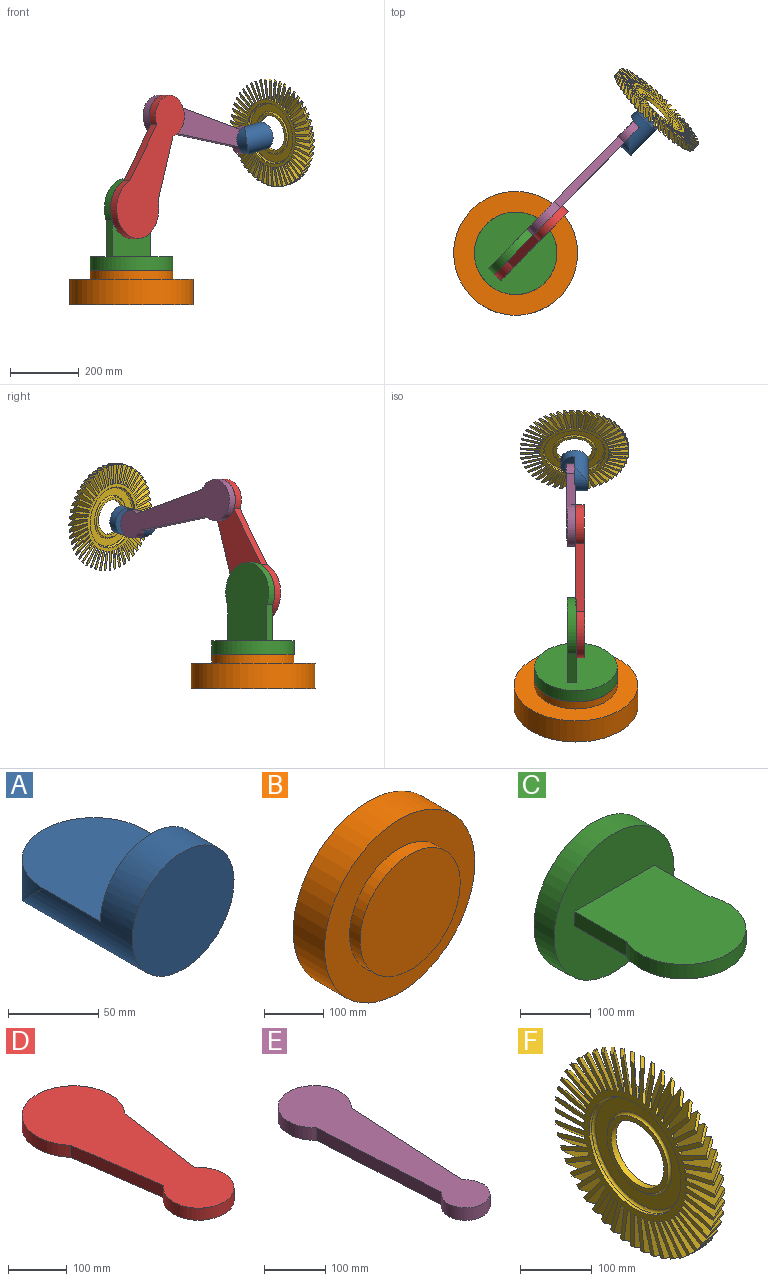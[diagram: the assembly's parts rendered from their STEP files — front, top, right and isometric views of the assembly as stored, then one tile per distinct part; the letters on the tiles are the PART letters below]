
ASSEMBLY  parts=6 mates=5
PART A: 5 faces, bbox 80x110x80 mm
  f0: plane 80x40mm, normal (0,1,0), area 2513.3mm2, adj f1,f3
  f1: cylinder r=40mm len=110mm, axis (0,-1,0), area 15138.1mm2, adj f0,f2,f3,f4
  f2: plane 80x80mm, normal (0,-1,0), area 5026.5mm2, adj f1
  f3: plane 85x80mm, normal (0,0,1), area 6113.3mm2, adj f0,f1,f4
  f4: cylinder r=40mm len=80mm, axis (0,0,1), area 3200mm2, adj f1,f3
PART B: 5 faces, bbox 360x100x360 mm
  f0: plane 240x240mm, normal (0,-1,0), area 45238.9mm2, adj f1
  f1: cylinder r=120mm len=240mm, axis (0,1,0), area 18849.6mm2, adj f0,f2
  f2: plane 360x360mm, normal (0,-1,0), area 56548.7mm2, adj f1,f3
  f3: cylinder r=180mm len=360mm, axis (0,1,0), area 84823mm2, adj f2,f4
  f4: plane 360x360mm, normal (0,1,0), area 101787.6mm2, adj f3
PART C: 8 faces, bbox 240x267.5x240 mm
  f0: plane 104.56x25mm, normal (-1,0,0), area 2613.9mm2, adj f1,f3,f4,f7
  f1: cylinder r=87.5mm len=175mm, axis (0,0,-1), area 8696.9mm2, adj f0,f2,f3,f4
  f2: plane 104.56x25mm, normal (1,0,0), area 2613.9mm2, adj f1,f3,f4,f7
  f3: plane 227.5x175mm, normal (0,0,1), area 34784mm2, adj f0,f1,f2,f7
  f4: plane 227.5x175mm, normal (0,0,-1), area 34784mm2, adj f0,f1,f2,f7
  f5: cylinder r=120mm len=240mm, axis (0,-1,0), area 30159.3mm2, adj f6,f7
  f6: plane 240x240mm, normal (0,1,0), area 45238.9mm2, adj f5
  f7: plane 240x240mm, normal (0,-1,0), area 41238.9mm2, adj f0,f2,f3,f4,f5
PART D: 6 faces, bbox 175x447.5x25 mm
  f0: cylinder r=87.5mm len=175mm, axis (0,0,1), area 10081.2mm2, adj f1,f3,f4,f5
  f1: plane 194.59x27.5mm, normal (-0.99,-0.14,0), area 4913mm2, adj f0,f2,f4,f5
  f2: cylinder r=60mm len=120mm, axis (0,0,1), area 7399.4mm2, adj f1,f3,f4,f5
  f3: plane 194.59x27.5mm, normal (0.99,-0.14,0), area 4913mm2, adj f0,f2,f4,f5
  f4: plane 447.5x175mm, normal (0,0,-1), area 52030.2mm2, adj f0,f1,f2,f3
  f5: plane 447.5x175mm, normal (0,0,1), area 52030.2mm2, adj f0,f1,f2,f3
PART E: 6 faces, bbox 120x450x25 mm
  f0: cylinder r=60mm len=120mm, axis (0,0,-1), area 7235.6mm2, adj f1,f3,f4,f5
  f1: plane 274.05x25mm, normal (-1,-0.05,0), area 6861.6mm2, adj f0,f2,f4,f5
  f2: cylinder r=40mm len=80mm, axis (0,0,-1), area 4932.9mm2, adj f1,f3,f4,f5
  f3: plane 274.05x25mm, normal (1,-0.05,0), area 6861.6mm2, adj f0,f2,f4,f5
  f4: plane 450x120mm, normal (0,0,1), area 33012mm2, adj f0,f1,f2,f3
  f5: plane 450x120mm, normal (0,0,-1), area 33012mm2, adj f0,f1,f2,f3
PART F: 209 faces, bbox 20.3x315.4x315.3 mm
  f0: torus R=86.5mm, axis (-1,0,0), area 3515.4mm2, adj f7,f203
  f1: torus R=64mm, axis (-1,0,0), area 2426.1mm2, adj f207,f208
  f2: torus R=64mm, axis (-1,0,0), area 2426.1mm2, adj f9,f203
  f3: cylinder r=157.5mm len=21.71mm, axis (1,0,0), area 130.3mm2, adj f6,f176,f177,f204
  f4: plane 22.36x20mm, normal (0,0.49,0.87), area 113.1mm2, adj f6,f12,f176,f204
  f5: cylinder r=157.5mm len=25.8mm, axis (1,0,0), area 130.3mm2, adj f6,f180,f204,f206
  f6: plane 314.98x314.86mm, normal (1,0,0), area 25655mm2, adj f3,f4,f5,f7,f12,f13,f14,f15
  f7: cylinder r=90.5mm len=181mm, axis (1,0,0), area 2843.1mm2, adj f0,f6
  f8: cylinder r=90.5mm len=181mm, axis (1,0,0), area 2843.1mm2, adj f11,f204
  f9: plane 120x120mm, normal (1,0,0), area 2814.9mm2, adj f2,f10
  f10: cylinder r=52mm len=104mm, axis (1,0,0), area 3267.3mm2, adj f9,f207
  f11: torus R=86.5mm, axis (-1,0,0), area 3515.5mm2, adj f8,f208
  f12: plane 61.08x41.82mm, normal (-0.71,0.64,-0.3), area 1610.9mm2, adj f4,f6,f19,f204
  f13: plane 24.82x20mm, normal (0,0.25,0.97), area 113.1mm2, adj f6,f14,f204,f206
  f14: plane 59.47x37.51mm, normal (0.71,-0.67,0.23), area 1598.6mm2, adj f6,f13,f15,f204
  f15: cylinder r=157.5mm len=24.84mm, axis (1,0,0), area 130.3mm2, adj f6,f14,f16,f204
  f16: plane 61.46x36.15mm, normal (-0.71,0.67,-0.22), area 1610.9mm2, adj f6,f15,f17,f204
  f17: plane 23.78x20mm, normal (0,0.38,0.93), area 113.1mm2, adj f6,f16,f18,f204
  f18: plane 59.11x43.29mm, normal (0.71,-0.64,0.31), area 1598.6mm2, adj f6,f17,f19,f204
  f19: cylinder r=157.5mm len=23.47mm, axis (1,0,0), area 130.3mm2, adj f6,f12,f18,f204
  f20: cylinder r=157.5mm len=26.34mm, axis (1,0,0), area 130.3mm2, adj f6,f21,f22,f204
  f21: plane 59.19x23.14mm, normal (-0.71,0.71,-0.04), area 1610.9mm2, adj f6,f20,f204,f205
  f22: plane 57.28x24.22mm, normal (0.71,-0.71,0.05), area 1598.6mm2, adj f6,f20,f181,f204
  f23: cylinder r=157.5mm len=26.45mm, axis (1,0,0), area 130.2mm2, adj f6,f24,f25,f204
  f24: plane 57.01x24.01mm, normal (-0.71,0.71,0.05), area 1610.9mm2, adj f6,f23,f181,f204
  f25: plane 58.43x23.45mm, normal (0.71,-0.71,-0.04), area 1598.6mm2, adj f6,f23,f202,f204
  f26: cylinder r=157.5mm len=26.13mm, axis (1,0,0), area 130.3mm2, adj f6,f27,f28,f204
  f27: plane 58.39x31.06mm, normal (-0.71,0.69,0.14), area 1610.9mm2, adj f6,f26,f202,f204
  f28: plane 60.04x30.2mm, normal (0.71,-0.7,-0.13), area 1598.6mm2, adj f6,f26,f155,f204
  f29: cylinder r=157.5mm len=25.37mm, axis (1,0,0), area 130.3mm2, adj f6,f30,f31,f204
  f30: plane 59.01x37.59mm, normal (-0.71,0.67,0.23), area 1610.9mm2, adj f6,f29,f155,f204
  f31: plane 60.71x36.48mm, normal (0.71,-0.67,-0.22), area 1598.6mm2, adj f6,f29,f201,f204
  f32: cylinder r=157.5mm len=24.2mm, axis (1,0,0), area 130.3mm2, adj f6,f33,f34,f204
  f33: plane 58.66x43.5mm, normal (-0.71,0.64,0.31), area 1610.9mm2, adj f6,f32,f201,f204
  f34: plane 60.38x42.17mm, normal (0.71,-0.64,-0.3), area 1598.6mm2, adj f6,f32,f156,f204
  f35: cylinder r=157.5mm len=22.63mm, axis (1,0,0), area 130.3mm2, adj f6,f36,f37,f204
  f36: plane 57.35x48.69mm, normal (-0.71,0.59,0.39), area 1610.9mm2, adj f6,f35,f156,f204
  f37: plane 59.07x47.18mm, normal (0.71,-0.6,-0.38), area 1598.6mm2, adj f6,f35,f200,f204
  f38: cylinder r=157.5mm len=20.69mm, axis (1,0,0), area 130.3mm2, adj f6,f39,f40,f204
  f39: plane 55.1x53.09mm, normal (-0.71,0.54,0.46), area 1610.9mm2, adj f6,f38,f200,f204
  f40: plane 56.8x51.41mm, normal (0.71,-0.54,-0.46), area 1598.6mm2, adj f6,f38,f157,f204
  f41: cylinder r=157.5mm len=20mm, axis (1,0,0), area 130.3mm2, adj f6,f42,f43,f204
  f42: plane 56.61x51.94mm, normal (-0.71,0.47,0.53), area 1610.9mm2, adj f6,f41,f157,f204
  f43: plane 54.81x53.59mm, normal (0.71,-0.48,-0.52), area 1601.4mm2, adj f6,f41,f199,f204
  f44: cylinder r=157.5mm len=21.21mm, axis (1,0,0), area 130.3mm2, adj f6,f45,f46,f204
  f45: plane 59.21x47.93mm, normal (-0.71,0.4,0.58), area 1610.9mm2, adj f6,f44,f199,f204
  f46: plane 57.3x49.52mm, normal (0.71,-0.41,-0.58), area 1601.4mm2, adj f6,f44,f158,f204
  f47: cylinder r=157.5mm len=23.06mm, axis (1,0,0), area 130.3mm2, adj f6,f48,f49,f204
  f48: plane 60.83x43.14mm, normal (-0.71,0.32,0.63), area 1610.9mm2, adj f6,f47,f158,f204
  f49: plane 58.87x44.63mm, normal (0.71,-0.33,-0.63), area 1601.4mm2, adj f6,f47,f198,f204
  f50: cylinder r=157.5mm len=24.53mm, axis (1,0,0), area 130.3mm2, adj f6,f51,f52,f204
  f51: plane 61.46x37.63mm, normal (-0.71,0.24,0.67), area 1610.9mm2, adj f6,f50,f198,f204
  f52: plane 59.47x39.02mm, normal (0.71,-0.25,-0.66), area 1601.4mm2, adj f6,f50,f159,f204
  f53: cylinder r=157.5mm len=25.6mm, axis (1,0,0), area 130.3mm2, adj f6,f54,f55,f204
  f54: plane 61.07x31.51mm, normal (-0.71,0.15,0.69), area 1610.9mm2, adj f6,f53,f159,f204
  f55: plane 59.1x32.77mm, normal (0.71,-0.16,-0.69), area 1601.4mm2, adj f6,f53,f197,f204
  f56: cylinder r=157.5mm len=26.25mm, axis (1,0,0), area 130.3mm2, adj f6,f57,f58,f204
  f57: plane 59.69x24.87mm, normal (-0.71,0.06,0.71), area 1610.9mm2, adj f6,f56,f197,f204
  f58: plane 57.76x25.98mm, normal (0.71,-0.07,-0.7), area 1601.4mm2, adj f6,f56,f160,f204
  f59: cylinder r=157.5mm len=26.47mm, axis (1,0,0), area 130.3mm2, adj f6,f60,f61,f204
  f60: plane 57.49x22.2mm, normal (-0.71,-0.03,0.71), area 1610.9mm2, adj f6,f59,f160,f204
  f61: plane 57.98x21.66mm, normal (0.71,0.02,-0.71), area 1601.4mm2, adj f6,f59,f196,f204
  f62: cylinder r=157.5mm len=26.25mm, axis (1,0,0), area 130.3mm2, adj f6,f63,f64,f204
  f63: plane 58.09x29.35mm, normal (-0.71,-0.12,0.7), area 1610.9mm2, adj f6,f62,f196,f204
  f64: plane 59.72x28.54mm, normal (0.71,0.11,-0.7), area 1601.4mm2, adj f6,f62,f161,f204
  f65: cylinder r=157.5mm len=25.6mm, axis (1,0,0), area 130.3mm2, adj f6,f66,f67,f204
  f66: plane 58.95x36.01mm, normal (-0.71,-0.21,0.68), area 1610.9mm2, adj f6,f65,f161,f204
  f67: plane 60.63x34.96mm, normal (0.71,0.2,-0.68), area 1601.4mm2, adj f6,f65,f195,f204
  f68: cylinder r=157.5mm len=24.53mm, axis (1,0,0), area 130.3mm2, adj f6,f69,f70,f204
  f69: plane 58.84x42.08mm, normal (-0.71,-0.29,0.65), area 1610.9mm2, adj f6,f68,f195,f204
  f70: plane 60.56x40.81mm, normal (0.71,0.28,-0.65), area 1601.4mm2, adj f6,f68,f162,f204
  f71: cylinder r=157.5mm len=23.06mm, axis (1,0,0), area 130.3mm2, adj f6,f72,f73,f204
  f72: plane 57.77x47.46mm, normal (-0.71,-0.37,0.6), area 1610.9mm2, adj f6,f71,f162,f204
  f73: plane 59.49x45.99mm, normal (0.71,0.36,-0.61), area 1601.4mm2, adj f6,f71,f194,f204
  f74: cylinder r=157.5mm len=21.21mm, axis (1,0,0), area 130.3mm2, adj f6,f75,f76,f204
  f75: plane 55.75x52.07mm, normal (-0.71,-0.45,0.55), area 1610.9mm2, adj f6,f74,f194,f204
  f76: plane 57.45x50.43mm, normal (0.71,0.44,-0.56), area 1601.4mm2, adj f6,f74,f163,f204
  f77: cylinder r=157.5mm len=20mm, axis (1,0,0), area 130.3mm2, adj f6,f78,f79,f204
  f78: plane 55.82x52.81mm, normal (-0.71,-0.51,0.49), area 1610.9mm2, adj f6,f77,f163,f204
  f79: plane 54.48x54.04mm, normal (0.71,0.51,-0.5), area 1601.4mm2, adj f6,f77,f193,f204
  f80: cylinder r=157.5mm len=20.7mm, axis (1,0,0), area 130.3mm2, adj f6,f81,f82,f204
  f81: plane 58.65x49.01mm, normal (-0.71,-0.57,0.42), area 1610.9mm2, adj f6,f80,f193,f204
  f82: plane 56.77x50.61mm, normal (0.71,0.56,-0.43), area 1601.4mm2, adj f6,f80,f164,f204
  f83: cylinder r=157.5mm len=22.64mm, axis (1,0,0), area 130.3mm2, adj f6,f84,f85,f204
  f84: plane 60.52x44.4mm, normal (-0.71,-0.62,0.34), area 1610.9mm2, adj f6,f83,f164,f204
  f85: plane 58.57x45.92mm, normal (0.71,0.61,-0.35), area 1601.4mm2, adj f6,f83,f192,f204
  f86: cylinder r=157.5mm len=24.2mm, axis (1,0,0), area 130.3mm2, adj f6,f87,f88,f204
  f87: plane 61.39x39.07mm, normal (-0.71,-0.66,0.26), area 1610.9mm2, adj f6,f86,f192,f204
  f88: plane 59.41x40.48mm, normal (0.71,0.65,-0.27), area 1601.4mm2, adj f6,f86,f165,f204
  f89: cylinder r=157.5mm len=25.37mm, axis (1,0,0), area 130.3mm2, adj f6,f90,f91,f204
  f90: plane 61.26x33.09mm, normal (-0.71,-0.69,0.18), area 1610.9mm2, adj f6,f89,f165,f204
  f91: plane 59.28x34.38mm, normal (0.71,0.68,-0.18), area 1601.4mm2, adj f6,f89,f191,f204
  f92: cylinder r=157.5mm len=26.13mm, axis (1,0,0), area 130.3mm2, adj f6,f93,f94,f204
  f93: plane 60.13x26.57mm, normal (-0.71,-0.7,0.09), area 1610.9mm2, adj f6,f92,f191,f204
  f94: plane 58.19x27.72mm, normal (0.71,0.7,-0.1), area 1601.4mm2, adj f6,f92,f166,f204
  f95: cylinder r=157.5mm len=26.45mm, axis (1,0,0), area 130.3mm2, adj f6,f96,f97,f204
  f96: plane 58.03x20.35mm, normal (-0.71,-0.71,0), area 1610.9mm2, adj f6,f95,f166,f204
  f97: plane 57.66x20.61mm, normal (0.71,0.71,0), area 1601.4mm2, adj f6,f95,f190,f204
  f98: cylinder r=157.5mm len=26.34mm, axis (1,0,0), area 130.3mm2, adj f6,f99,f100,f204
  f99: plane 57.72x27.6mm, normal (-0.71,-0.7,-0.1), area 1610.9mm2, adj f6,f98,f190,f204
  f100: plane 59.33x26.86mm, normal (0.71,0.7,0.09), area 1601.4mm2, adj f6,f98,f167,f204
  f101: cylinder r=157.5mm len=25.8mm, axis (1,0,0), area 130.3mm2, adj f6,f102,f103,f204
  f102: plane 58.82x34.39mm, normal (-0.71,-0.68,-0.18), area 1610.9mm2, adj f6,f101,f167,f204
  f103: plane 60.49x33.41mm, normal (0.71,0.69,0.18), area 1601.4mm2, adj f6,f101,f189,f204
  f104: cylinder r=157.5mm len=24.84mm, axis (1,0,0), area 130.3mm2, adj f6,f105,f106,f204
  f105: plane 58.96x40.62mm, normal (-0.71,-0.65,-0.27), area 1610.9mm2, adj f6,f104,f189,f204
  f106: plane 60.67x39.41mm, normal (0.71,0.66,0.26), area 1601.4mm2, adj f6,f104,f168,f204
  f107: cylinder r=157.5mm len=23.46mm, axis (1,0,0), area 130.3mm2, adj f6,f108,f109,f204
  f108: plane 58.13x46.19mm, normal (-0.71,-0.61,-0.35), area 1610.9mm2, adj f6,f107,f168,f204
  f109: plane 59.85x44.77mm, normal (0.71,0.62,0.34), area 1601.4mm2, adj f6,f107,f188,f204
  f110: cylinder r=157.5mm len=21.7mm, axis (1,0,0), area 130.3mm2, adj f6,f111,f112,f204
  f111: plane 56.34x50.99mm, normal (-0.71,-0.56,-0.43), area 1610.9mm2, adj f6,f110,f188,f204
  f112: plane 58.05x49.39mm, normal (0.71,0.57,0.42), area 1601.4mm2, adj f6,f110,f169,f204
  f113: cylinder r=157.5mm len=20mm, axis (1,0,0), area 130.3mm2, adj f6,f114,f115,f204
  f114: plane 54.96x53.63mm, normal (-0.71,-0.51,-0.5), area 1610.9mm2, adj f6,f113,f169,f204
  f115: plane 55.31x53.22mm, normal (0.71,0.51,0.49), area 1601.4mm2, adj f6,f113,f187,f204
  f116: cylinder r=157.5mm len=20.16mm, axis (1,0,0), area 130.3mm2, adj f6,f117,f118,f204
  f117: plane 58.03x50.04mm, normal (-0.71,-0.44,-0.56), area 1610.9mm2, adj f6,f116,f187,f204
  f118: plane 56.17x51.66mm, normal (0.71,0.45,0.55), area 1598.6mm2, adj f6,f116,f170,f204
  f119: cylinder r=157.5mm len=22.18mm, axis (1,0,0), area 130.3mm2, adj f6,f120,f121,f204
  f120: plane 60.14x45.63mm, normal (-0.71,-0.36,-0.61), area 1610.9mm2, adj f6,f119,f170,f204
  f121: plane 58.21x47.17mm, normal (0.71,0.37,0.6), area 1598.6mm2, adj f6,f119,f186,f204
  f122: cylinder r=157.5mm len=23.85mm, axis (1,0,0), area 130.3mm2, adj f6,f123,f124,f204
  f123: plane 61.27x40.47mm, normal (-0.71,-0.28,-0.65), area 1610.9mm2, adj f6,f122,f186,f204
  f124: plane 59.29x41.91mm, normal (0.71,0.29,0.65), area 1598.6mm2, adj f6,f122,f171,f204
  f125: cylinder r=157.5mm len=25.12mm, axis (1,0,0), area 130.3mm2, adj f6,f126,f127,f204
  f126: plane 61.39x34.64mm, normal (-0.71,-0.2,-0.68), area 1610.9mm2, adj f6,f125,f171,f204
  f127: plane 59.41x35.96mm, normal (0.71,0.21,0.68), area 1598.6mm2, adj f6,f125,f185,f204
  f128: cylinder r=157.5mm len=25.98mm, axis (1,0,0), area 130.3mm2, adj f6,f129,f130,f204
  f129: plane 60.5x28.25mm, normal (-0.71,-0.11,-0.7), area 1610.9mm2, adj f6,f128,f185,f204
  f130: plane 58.55x29.43mm, normal (0.71,0.12,0.7), area 1598.6mm2, adj f6,f128,f172,f204
  f131: cylinder r=157.5mm len=26.41mm, axis (1,0,0), area 130.3mm2, adj f6,f132,f133,f204
  f132: plane 58.63x21.39mm, normal (-0.71,-0.02,-0.71), area 1610.9mm2, adj f6,f131,f172,f204
  f133: plane 57.42x22.43mm, normal (0.71,0.03,0.71), area 1598.6mm2, adj f6,f131,f184,f204
  f134: cylinder r=157.5mm len=26.41mm, axis (1,0,0), area 130.3mm2, adj f6,f135,f136,f204
  f135: plane 57.35x25.83mm, normal (-0.71,0.07,-0.7), area 1610.9mm2, adj f6,f134,f184,f204
  f136: plane 58.89x25.15mm, normal (0.71,-0.06,0.71), area 1598.6mm2, adj f6,f134,f173,f204
  f137: cylinder r=157.5mm len=25.98mm, axis (1,0,0), area 130.3mm2, adj f6,f138,f139,f204
  f138: plane 58.64x32.74mm, normal (-0.71,0.16,-0.69), area 1610.9mm2, adj f6,f137,f173,f204
  f139: plane 60.3x31.82mm, normal (0.71,-0.15,0.69), area 1598.6mm2, adj f6,f137,f183,f204
  f140: cylinder r=157.5mm len=25.12mm, axis (1,0,0), area 130.3mm2, adj f6,f141,f142,f204
  f141: plane 59.02x39.13mm, normal (-0.71,0.25,-0.66), area 1610.9mm2, adj f6,f140,f183,f204
  f142: plane 60.72x37.96mm, normal (0.71,-0.24,0.67), area 1598.6mm2, adj f6,f140,f174,f204
  f143: cylinder r=157.5mm len=23.84mm, axis (1,0,0), area 130.3mm2, adj f6,f144,f145,f204
  f144: plane 58.43x44.86mm, normal (-0.71,0.33,-0.63), area 1610.9mm2, adj f6,f143,f174,f204
  f145: plane 60.15x43.49mm, normal (0.71,-0.32,0.63), area 1598.6mm2, adj f6,f143,f182,f204
  f146: cylinder r=157.5mm len=22.18mm, axis (1,0,0), area 130.3mm2, adj f6,f147,f148,f204
  f147: plane 56.88x49.87mm, normal (-0.71,0.41,-0.58), area 1610.9mm2, adj f6,f146,f182,f204
  f148: plane 58.59x48.31mm, normal (0.71,-0.4,0.58), area 1598.6mm2, adj f6,f146,f175,f204
  f149: cylinder r=157.5mm len=20.15mm, axis (1,0,0), area 130.3mm2, adj f6,f150,f151,f204
  f150: plane 54.39x54.05mm, normal (-0.71,0.48,-0.52), area 1610.9mm2, adj f6,f149,f175,f204
  f151: plane 56.08x52.34mm, normal (0.71,-0.47,0.53), area 1598.6mm2, adj f6,f149,f179,f204
  f152: cylinder r=157.5mm len=20mm, axis (1,0,0), area 130.3mm2, adj f6,f153,f154,f204
  f153: plane 57.35x51.02mm, normal (-0.71,0.54,-0.46), area 1610.9mm2, adj f6,f152,f179,f204
  f154: plane 55.52x52.65mm, normal (0.71,-0.54,0.46), area 1598.6mm2, adj f6,f152,f178,f204
  f155: plane 24.82x20mm, normal (0,-0.25,0.97), area 113.1mm2, adj f6,f28,f30,f204
  f156: plane 22.36x20mm, normal (0,-0.49,0.87), area 113.1mm2, adj f6,f34,f36,f204
  f157: plane 20x18.43mm, normal (0,-0.7,0.72), area 113.1mm2, adj f6,f40,f42,f204
  f158: plane 21.94x20mm, normal (0,-0.86,0.52), area 113.1mm2, adj f6,f46,f48,f204
  f159: plane 24.6x20mm, normal (0,-0.96,0.28), area 113.1mm2, adj f6,f52,f54,f204
  f160: plane 25.64x20mm, normal (0,-1,0.03), area 113.1mm2, adj f6,f58,f60,f204
  f161: plane 25.01x20mm, normal (0,-0.97,-0.22), area 113.1mm2, adj f6,f64,f66,f204
  f162: plane 22.75x20mm, normal (0,-0.89,-0.46), area 113.1mm2, adj f6,f70,f72,f204
  f163: plane 20x18.99mm, normal (0,-0.74,-0.67), area 113.1mm2, adj f6,f76,f78,f204
  f164: plane 21.5x20mm, normal (0,-0.55,-0.84), area 113.1mm2, adj f6,f82,f84,f204
  f165: plane 24.35x20mm, normal (0,-0.32,-0.95), area 113.1mm2, adj f6,f88,f90,f204
  f166: plane 25.6x20mm, normal (0,-0.06,-1), area 113.1mm2, adj f6,f94,f96,f204
  f167: plane 25.18x20mm, normal (0,0.19,-0.98), area 113.1mm2, adj f6,f100,f102,f204
  f168: plane 23.12x20mm, normal (0,0.43,-0.9), area 113.1mm2, adj f6,f106,f108,f204
  f169: plane 20x19.54mm, normal (0,0.65,-0.76), area 113.1mm2, adj f6,f112,f114,f204
  f170: plane 21.04x20mm, normal (0,0.82,-0.57), area 113.1mm2, adj f6,f118,f120,f204
  f171: plane 24.08x20mm, normal (0,0.94,-0.35), area 113.1mm2, adj f6,f124,f126,f204
  f172: plane 25.54x20mm, normal (0,1,-0.1), area 113.1mm2, adj f6,f130,f132,f204
  f173: plane 25.33x20mm, normal (0,0.99,0.16), area 113.1mm2, adj f6,f136,f138,f204
  f174: plane 23.46x20mm, normal (0,0.91,0.4), area 113.1mm2, adj f6,f142,f144,f204
  f175: plane 20.06x20mm, normal (0,0.78,0.62), area 113.1mm2, adj f6,f148,f150,f204
  f176: plane 57.78x48.37mm, normal (0.71,-0.59,0.39), area 1598.6mm2, adj f3,f4,f6,f204
  f177: plane 59.71x46.8mm, normal (-0.71,0.6,-0.38), area 1610.9mm2, adj f3,f6,f178,f204
  f178: plane 20.56x20mm, normal (0,0.6,0.8), area 113.1mm2, adj f6,f154,f177,f204
  f179: plane 20x18.43mm, normal (0,0.7,0.72), area 113.1mm2, adj f6,f151,f153,f204
  f180: plane 58.57x30.83mm, normal (0.71,-0.69,0.14), area 1598.6mm2, adj f5,f6,f204,f205
  f181: plane 25.66x20mm, normal (0,0,1), area 113.1mm2, adj f6,f22,f24,f204
  f182: plane 21.94x20mm, normal (0,0.86,0.52), area 113.1mm2, adj f6,f145,f147,f204
  f183: plane 24.6x20mm, normal (0,0.96,0.28), area 113.1mm2, adj f6,f139,f141,f204
  f184: plane 25.64x20mm, normal (0,1,0.03), area 113.1mm2, adj f6,f133,f135,f204
  f185: plane 25.01x20mm, normal (0,0.97,-0.22), area 113.1mm2, adj f6,f127,f129,f204
  f186: plane 22.75x20mm, normal (0,0.89,-0.46), area 113.1mm2, adj f6,f121,f123,f204
  f187: plane 20x18.99mm, normal (0,0.74,-0.67), area 113.1mm2, adj f6,f115,f117,f204
  f188: plane 21.5x20mm, normal (0,0.55,-0.84), area 113.1mm2, adj f6,f109,f111,f204
  f189: plane 24.35x20mm, normal (0,0.32,-0.95), area 113.1mm2, adj f6,f103,f105,f204
  f190: plane 25.6x20mm, normal (0,0.06,-1), area 113.1mm2, adj f6,f97,f99,f204
  f191: plane 25.18x20mm, normal (0,-0.19,-0.98), area 113.1mm2, adj f6,f91,f93,f204
  f192: plane 23.12x20mm, normal (0,-0.43,-0.9), area 113.1mm2, adj f6,f85,f87,f204
  f193: plane 20x19.54mm, normal (0,-0.65,-0.76), area 113.1mm2, adj f6,f79,f81,f204
  f194: plane 21.04x20mm, normal (0,-0.82,-0.57), area 113.1mm2, adj f6,f73,f75,f204
  f195: plane 24.08x20mm, normal (0,-0.94,-0.35), area 113.1mm2, adj f6,f67,f69,f204
  f196: plane 25.54x20mm, normal (0,-1,-0.1), area 113.1mm2, adj f6,f61,f63,f204
  f197: plane 25.33x20mm, normal (0,-0.99,0.16), area 113.1mm2, adj f6,f55,f57,f204
  f198: plane 23.46x20mm, normal (0,-0.91,0.4), area 113.1mm2, adj f6,f49,f51,f204
  f199: plane 20.06x20mm, normal (0,-0.78,0.62), area 113.1mm2, adj f6,f43,f45,f204
  f200: plane 20.56x20mm, normal (0,-0.6,0.8), area 113.1mm2, adj f6,f37,f39,f204
  f201: plane 23.78x20mm, normal (0,-0.38,0.93), area 113.1mm2, adj f6,f31,f33,f204
  f202: plane 25.45x20mm, normal (0,-0.13,0.99), area 113.1mm2, adj f6,f25,f27,f204
  f203: plane 173.06x173mm, normal (1,0,0), area 10638.2mm2, adj f0,f2
  f204: plane 314.98x314.85mm, normal (-1,0,0), area 25230.4mm2, adj f3,f4,f5,f8,f12,f13,f14,f15
  f205: plane 25.45x20mm, normal (0,0.13,0.99), area 113.1mm2, adj f6,f21,f180,f204
  f206: plane 60.82x29.89mm, normal (-0.71,0.7,-0.13), area 1610.9mm2, adj f5,f6,f13,f204
  f207: plane 120x120mm, normal (-1,0,0), area 2814.9mm2, adj f1,f10
  f208: plane 176.2x173mm, normal (-1,0,0), area 10638.2mm2, adj f1,f11
PLACE A rot(axis=(-0.72,0.22,0.66),141.4deg) t=(381.87,387.92,492.15)mm
PLACE B rot(axis=(-1,0,0),90deg) t=(0,0,1030)mm
PLACE C rot(axis=(-0.86,-0.36,0.36),98.6deg) t=(0,0,1030)mm
PLACE D rot(axis=(-0.85,-0.14,0.51),110.1deg) t=(232.94,236.63,952.49)mm
PLACE E rot(axis=(-0.64,0.34,0.69),156.9deg) t=(402.42,408.78,458.49)mm
PLACE F rot(axis=(-0.84,-0.45,0.28),95deg) t=(405.96,412.39,498.92)mm
MATE fastened A.f1 <-> F.f3  axis (0.69,0.7,0.19) through (381.87,387.92,492.15)mm
MATE revolute B.f1 <-> C.f5  axis (0,0,1) through (0,0,100)mm
MATE revolute E.f2 <-> A.f4  axis (0.71,-0.7,0) through (333.7,338.98,478.6)mm
MATE revolute D.f0 <-> C.f1  axis (-0.71,0.7,0) through (0,0,280)mm
MATE revolute E.f0 <-> D.f2  axis (0.71,-0.7,0) through (93.18,94.65,549)mm
